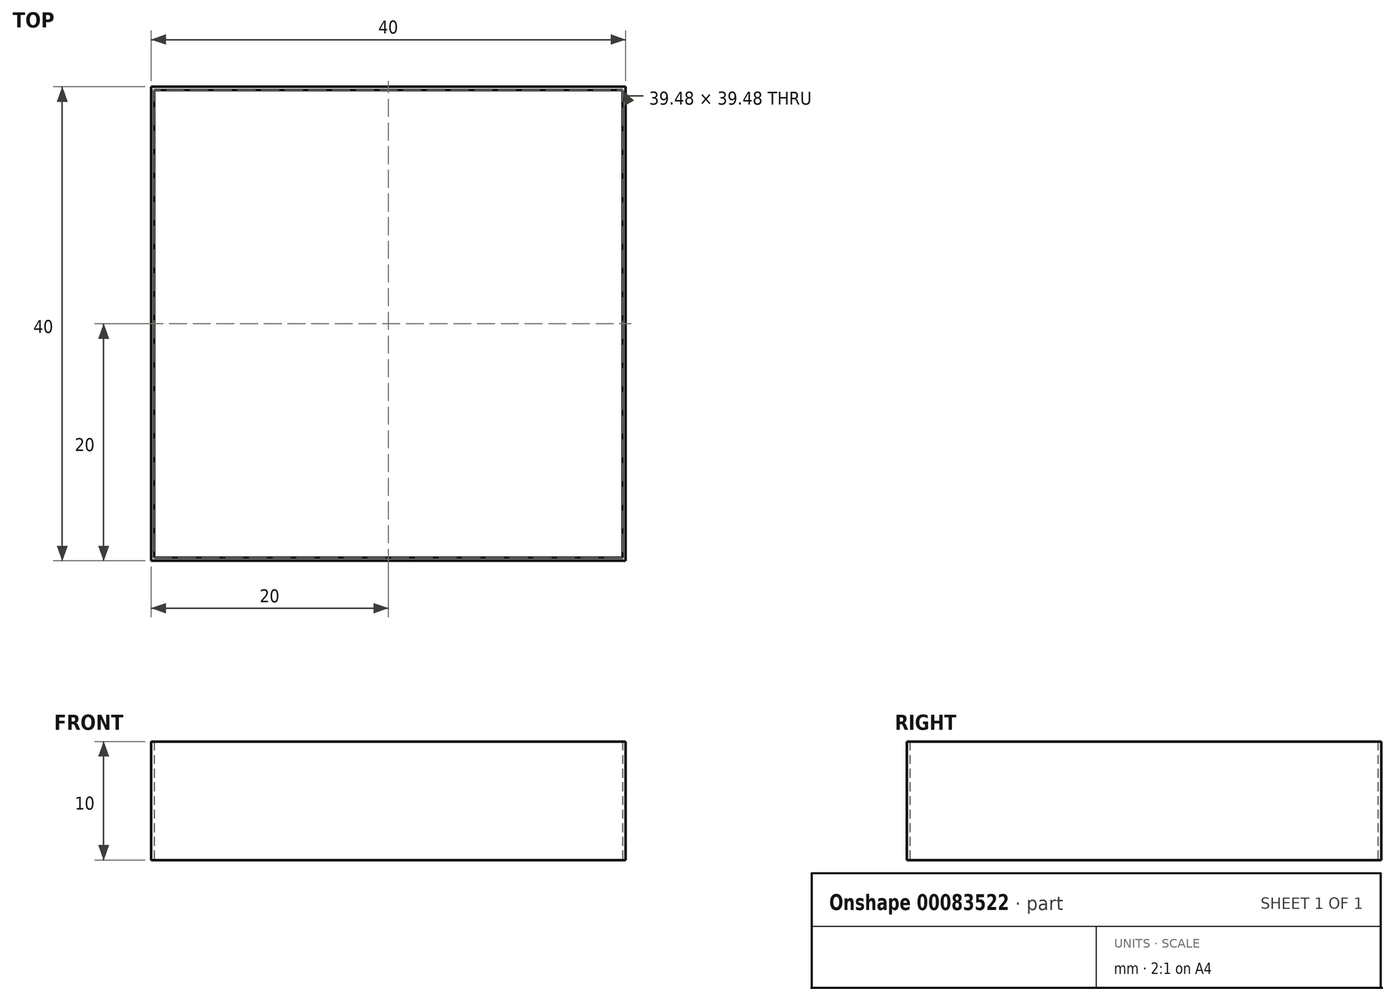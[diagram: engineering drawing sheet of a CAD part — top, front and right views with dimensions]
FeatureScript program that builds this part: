
annotation { "Feature Type Name" : "Feature", "Feature Type Description" : "" }
export const myFeature = defineFeature(function(context is Context, id is Id, definition is map)
    precondition{}
    {
        {
            var Q0;
            Q0=qCreatedBy(makeId("Top.planeOp"),FACE);
            var sketch = newSketch(context, id + "F0", { "sketchPlane" : qUnion([Q0])});
            skLineSegment(sketch, "E0.bottom", {"start": v(20, -20) * mm, "end": v(-20, -20) * mm});
            skLineSegment(sketch, "E0.top", {"start": v(20, 20) * mm, "end": v(-20, 20) * mm});
            skLineSegment(sketch, "E0.left", {"start": v(20, -20) * mm, "end": v(20, 20) * mm});
            skLineSegment(sketch, "E0.right", {"start": v(-20, -20) * mm, "end": v(-20, 20) * mm});
            skPoint(sketch, "E0.middle", {"position": v(0, 0) * mm});
            skLineSegment(sketch, "E1.0", {"start": v(19.74, 19.74) * mm, "end": v(-19.74, 19.74) * mm});
            skLineSegment(sketch, "E1.1", {"start": v(19.74, -19.74) * mm, "end": v(19.74, 19.74) * mm});
            skLineSegment(sketch, "E1.2", {"start": v(19.74, -19.74) * mm, "end": v(-19.74, -19.74) * mm});
            skLineSegment(sketch, "E1.3", {"start": v(-19.74, -19.74) * mm, "end": v(-19.74, 19.74) * mm});
            skSolve(sketch);
        }
        {
            var Q0;
            Q0=makeQuery(id+"F0.imprint","IMPRINT",FACE,{"disambiguationData":[TD([[makeQuery(id+"F0.imprint","IMPRINT",EDGE,{"derivedFrom":sQuery(id+"F0.wireOp",EDGE,"E0.bottom")}),-1.0]])]});
            extrude(context, id + "F1", {"entities" : qUnion([Q0]), "depth" : 10 * mm});
        }
    });
